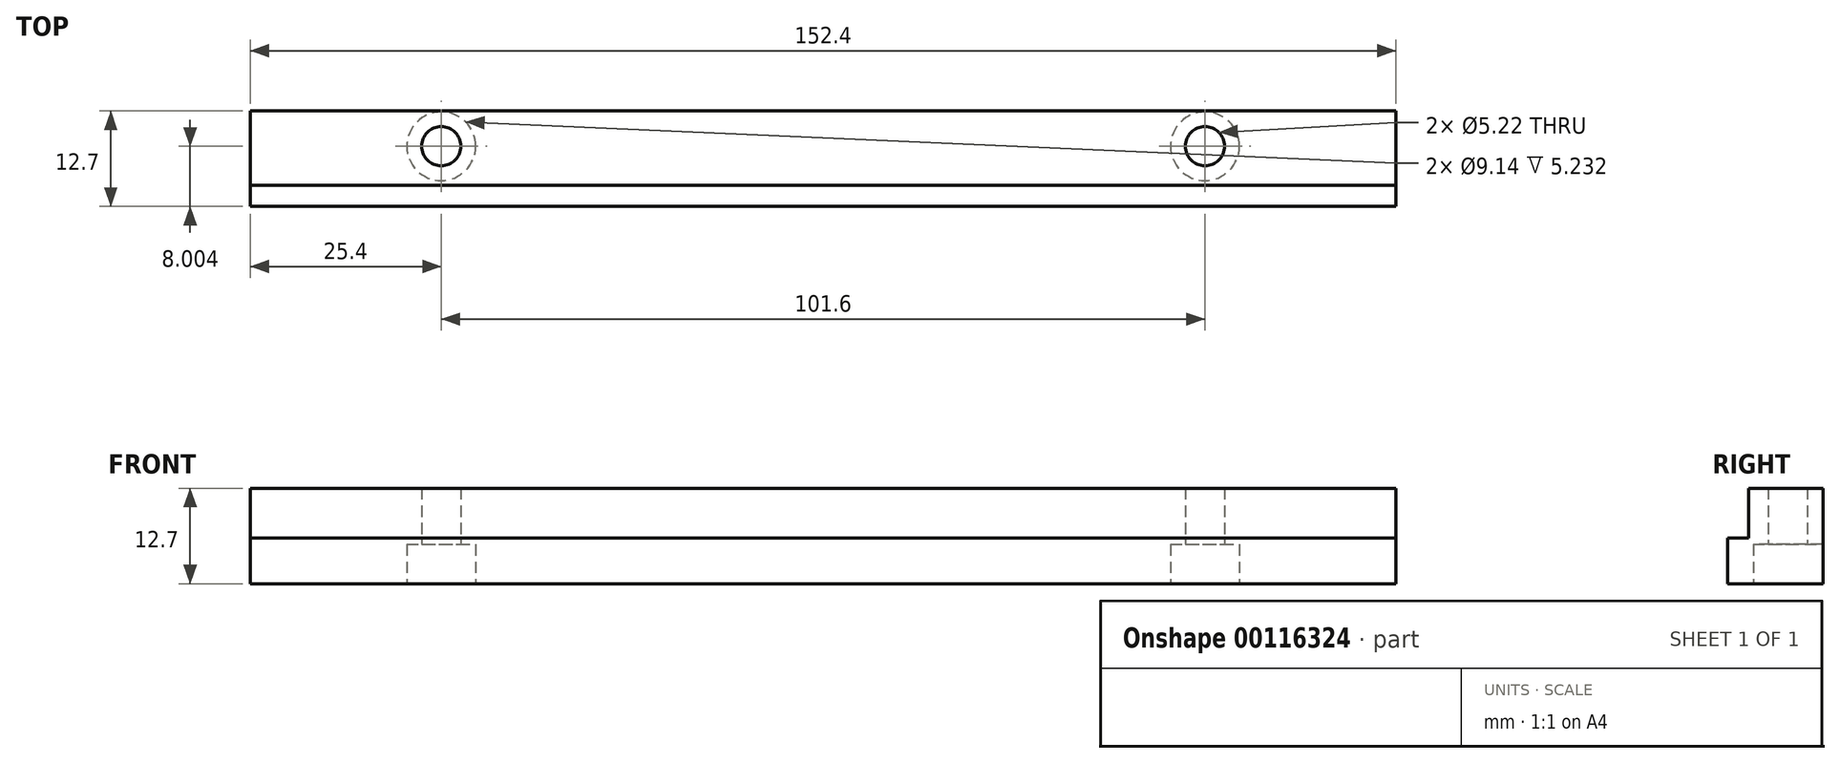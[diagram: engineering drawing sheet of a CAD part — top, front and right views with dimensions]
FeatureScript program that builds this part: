
annotation { "Feature Type Name" : "Feature", "Feature Type Description" : "" }
export const myFeature = defineFeature(function(context is Context, id is Id, definition is map)
    precondition{}
    {
        {
            var Q0;
            Q0=qCreatedBy(makeId("Right.planeOp"),FACE);
            var sketch = newSketch(context, id + "F0", { "sketchPlane" : qUnion([Q0])});
            skLineSegment(sketch, "E0.bottom", {"start": v(-4.95, 6.35) * mm, "end": v(4.95, 6.35) * mm});
            skLineSegment(sketch, "E0.left", {"start": v(-4.95, 6.35) * mm, "end": v(-4.95, -0.25) * mm});
            skLineSegment(sketch, "E0.right", {"start": v(4.95, 6.35) * mm, "end": v(4.95, -6.35) * mm});
            skLineSegment(sketch, "E1.bottom", {"start": v(-4.95, -0.25) * mm, "end": v(-7.75, -0.25) * mm});
            skLineSegment(sketch, "E1.top", {"start": v(4.95, -6.35) * mm, "end": v(-7.75, -6.35) * mm});
            skLineSegment(sketch, "E1.right", {"start": v(-7.75, -0.25) * mm, "end": v(-7.75, -6.35) * mm});
            skPoint(sketch, "E2", {"position": v(4.95, 0) * mm});
            skPoint(sketch, "E3", {"position": v(0, 6.35) * mm});
            skSolve(sketch);
        }
        {
            var Q0;
            Q0 = qSketchRegion(id + "F0", true);
            extrude(context, id + "F1", {"entities" : qUnion([Q0]), "endBound" : BoundingType.SYMMETRIC, "depth" : 152.4 * mm});
        }
        {
            var Q0;
            Q0=makeQuery(id+"F1.opExtrude","SWEPT_FACE",FACE,{"disambiguationData":[OSD([sQuery(id+"F0.wireOp",EDGE,"E1.top")])]});
            var sketch = newSketch(context, id + "F2", { "sketchPlane" : qUnion([Q0])});
            skPoint(sketch, "E4", {"position": v(-50.8, -0.25) * mm});
            skPoint(sketch, "E5", {"position": v(50.8, -0.25) * mm});
            skSolve(sketch);
        }
        {
            var Q0;
            Q0=sQuery(id+"F2.wireOp",VERTEX,"E4");
            var Q1;
            Q1=sQuery(id+"F2.wireOp",VERTEX,"E5");
            var Q2;
            Q2=makeQuery(id+"F1.opExtrude","SWEPT_BODY",BODY,{"disambiguationData":[OSD([sQuery(id+"F0.wireOp",EDGE,"E0.bottom"),sQuery(id+"F0.wireOp",EDGE,"E0.left"),sQuery(id+"F0.wireOp",EDGE,"E0.right"),sQuery(id+"F0.wireOp",EDGE,"E1.bottom"),sQuery(id+"F0.wireOp",EDGE,"E1.top"),sQuery(id+"F0.wireOp",EDGE,"E1.right")])]});
            hole(context, id + "F3", {"style" : HoleStyle.C_BORE, "endStyle" : HoleEndStyle.THROUGH, "holeDiameter" : 5.22 * mm, "cBoreDiameter" : 9.14 * mm, "cBoreDepth" : 5.23 * mm, "locations" : qUnion([Q0, Q1]), "scope" : qUnion([Q2]), "isTappedThrough" : true});
        }
    });
